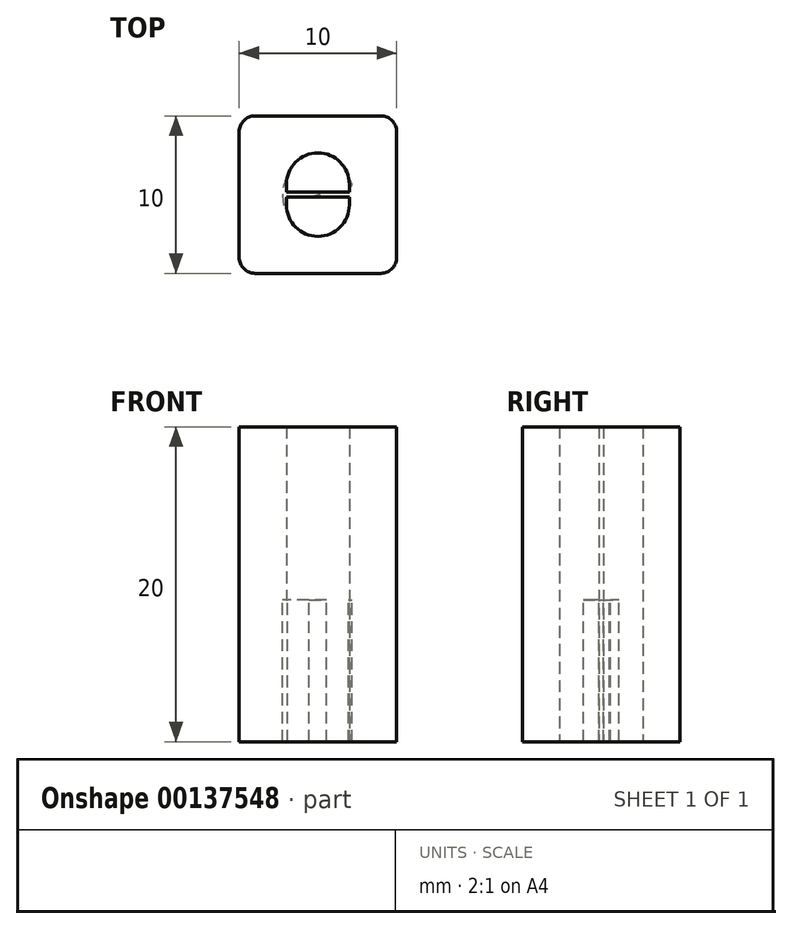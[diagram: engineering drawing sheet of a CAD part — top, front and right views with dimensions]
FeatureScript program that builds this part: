
annotation { "Feature Type Name" : "Feature", "Feature Type Description" : "" }
export const myFeature = defineFeature(function(context is Context, id is Id, definition is map)
    precondition{}
    {
        {
            var Q0;
            Q0=qCreatedBy(makeId("Top.planeOp"),FACE);
            var sketch = newSketch(context, id + "F0", { "sketchPlane" : qUnion([Q0])});
            skLineSegment(sketch, "E0.rect.bottom", {"start": v(4.45, -5.07) * mm, "end": v(-5.55, -5.07) * mm});
            skLineSegment(sketch, "E0.rect.top", {"start": v(4.45, 4.93) * mm, "end": v(-5.55, 4.93) * mm});
            skLineSegment(sketch, "E0.rect.left", {"start": v(4.45, -5.07) * mm, "end": v(4.45, 4.93) * mm});
            skLineSegment(sketch, "E0.rect.right", {"start": v(-5.55, -5.07) * mm, "end": v(-5.55, 4.93) * mm});
            skPoint(sketch, "E0.rect.middle", {"position": v(-0.55, -0.07) * mm});
            skLineSegment(sketch, "E1.rect.bottom", {"start": v(1.45, -0.22) * mm, "end": v(-2.55, -0.22) * mm});
            skLineSegment(sketch, "E1.rect.top", {"start": v(1.45, 0.08) * mm, "end": v(-2.55, 0.08) * mm});
            skLineSegment(sketch, "E1.rect.left", {"start": v(1.45, -0.22) * mm, "end": v(1.45, 0.08) * mm});
            skLineSegment(sketch, "E1.rect.right", {"start": v(-2.55, -0.22) * mm, "end": v(-2.55, 0.08) * mm});
            skLineSegment(sketch, "E2.bottom", {"start": v(-2.55, -0.22) * mm, "end": v(1.45, -0.22) * mm});
            skLineSegment(sketch, "E2.left", {"start": v(-2.55, -0.22) * mm, "end": v(-2.55, -0.72) * mm});
            skLineSegment(sketch, "E2.right", {"start": v(1.45, -0.22) * mm, "end": v(1.45, -0.72) * mm});
            skLineSegment(sketch, "E3.bottom", {"start": v(-2.55, 0.08) * mm, "end": v(1.45, 0.08) * mm});
            skLineSegment(sketch, "E3.left", {"start": v(-2.55, 0.08) * mm, "end": v(-2.55, 0.58) * mm});
            skLineSegment(sketch, "E3.right", {"start": v(1.45, 0.08) * mm, "end": v(1.45, 0.58) * mm});
            skArc(sketch, "E4", {"start": v(-2.55, -0.72) * mm, "mid": v(-0.55, -2.72) * mm, "end": v(1.45, -0.72) * mm});
            skArc(sketch, "E5", {"start": v(1.45, 0.58) * mm, "mid": v(-0.55, 2.58) * mm, "end": v(-2.55, 0.58) * mm});
            skLineSegment(sketch, "E6", {"start": v(-0.55, -5.07) * mm, "end": v(-0.55, 4.93) * mm, "construction": true});
            skSolve(sketch);
        }
        {
            var Q0;
            Q0=makeQuery(id+"F0.imprint","IMPRINT",FACE,{"disambiguationData":[TD([[makeQuery(id+"F0.imprint","IMPRINT",EDGE,{"derivedFrom":sQuery(id+"F0.wireOp",EDGE,"E0.rect.bottom")}),-1.0]])]});
            var Q1;
            Q1=makeQuery(id+"F0.imprint","IMPRINT",FACE,{"disambiguationData":[TD([[makeQuery(id+"F0.imprint","IMPRINT",EDGE,{"derivedFrom":sQuery(id+"F0.wireOp",EDGE,"E1.rect.left")}),1.0]])]});
            extrude(context, id + "F1", {"entities" : qUnion([Q0, Q1]), "depth" : 9 * mm});
        }
        {
            var Q0;
            Q0=makeQuery(id+"F0.imprint","IMPRINT",FACE,{"disambiguationData":[TD([[makeQuery(id+"F0.imprint","IMPRINT",EDGE,{"derivedFrom":sQuery(id+"F0.wireOp",EDGE,"E0.rect.bottom")}),-1.0]])]});
            var Q1;
            Q1=makeQuery(id+"F0.imprint","IMPRINT",FACE,{"disambiguationData":[TD([[makeQuery(id+"F0.imprint","IMPRINT",EDGE,{"derivedFrom":sQuery(id+"F0.wireOp",EDGE,"E2.bottom")}),-1.0]])]});
            var Q2;
            Q2=makeQuery(id+"F0.imprint","IMPRINT",FACE,{"disambiguationData":[TD([[makeQuery(id+"F0.imprint","IMPRINT",EDGE,{"derivedFrom":sQuery(id+"F0.wireOp",EDGE,"E1.rect.left")}),1.0]])]});
            var Q3;
            Q3=makeQuery(id+"F0.imprint","IMPRINT",FACE,{"disambiguationData":[TD([[makeQuery(id+"F0.imprint","IMPRINT",EDGE,{"derivedFrom":sQuery(id+"F0.wireOp",EDGE,"E3.bottom")}),1.0]])]});
            extrude(context, id + "F2", {"entities" : qUnion([Q0, Q1, Q2, Q3]), "operationType" : NewBodyOperationType.ADD, "oppositeDirection" : true, "depth" : 2 * mm});
        }
        {
            var Q0;
            Q0=makeQuery(id+"F2.opExtrude","CAP_FACE",FACE,{"disambiguationData":[OSD([sQuery(id+"F0.wireOp",EDGE,"E0.rect.bottom"),sQuery(id+"F0.wireOp",EDGE,"E0.rect.top"),sQuery(id+"F0.wireOp",EDGE,"E0.rect.left"),sQuery(id+"F0.wireOp",EDGE,"E0.rect.right")])],"isStart":false});
            var sketch = newSketch(context, id + "F3", { "sketchPlane" : qUnion([Q0])});
            skCircle(sketch, "E7", {"center": v(-0.55, 0.07) * mm, "radius": 2.25 * mm});
            skLineSegment(sketch, "E8", {"start": v(-0.55, 5.07) * mm, "end": v(-0.55, -4.93) * mm, "construction": true});
            skLineSegment(sketch, "E9", {"start": v(-2.72, 0.66) * mm, "end": v(1.63, -0.5) * mm});
            skSolve(sketch);
        }
        {
            var Q0;
            Q0=makeQuery(id+"F3.imprint","IMPRINT",FACE,{"disambiguationData":[TD([[makeQuery(id+"F3.imprint","IMPRINT",EDGE,{"derivedFrom":makeQuery(id+"F2.opExtrude","CAP_EDGE",EDGE,{"disambiguationData":[OSD([sQuery(id+"F0.wireOp",EDGE,"E0.rect.bottom")])],"isStart":false})}),1.0]])]});
            var Q1;
            {var subQ0=sQuery(id+"F3.wireOp",EDGE,"E9");Q1=makeQuery(id+"F3.imprint","IMPRINT",FACE,{"disambiguationData":[TD([[makeQuery(id+"F3.imprint","IMPRINT",EDGE,{"derivedFrom":subQ0}),1.0]])]});}
            extrude(context, id + "F4", {"entities" : qUnion([Q0, Q1]), "depth" : 9 * mm});
        }
        {
            var Q0;
            Q0=makeQuery(id+"F1.opExtrude","SWEPT_BODY",BODY,{"disambiguationData":[OSD([sQuery(id+"F0.wireOp",EDGE,"E0.rect.bottom"),sQuery(id+"F0.wireOp",EDGE,"E0.rect.top"),sQuery(id+"F0.wireOp",EDGE,"E0.rect.left"),sQuery(id+"F0.wireOp",EDGE,"E0.rect.right"),sQuery(id+"F0.wireOp",EDGE,"E2.bottom"),sQuery(id+"F0.wireOp",EDGE,"E2.left"),sQuery(id+"F0.wireOp",EDGE,"E2.right"),sQuery(id+"F0.wireOp",EDGE,"E3.bottom"),sQuery(id+"F0.wireOp",EDGE,"E3.left"),sQuery(id+"F0.wireOp",EDGE,"E3.right"),sQuery(id+"F0.wireOp",EDGE,"E4"),sQuery(id+"F0.wireOp",EDGE,"E5")])]});
            var Q1;
            Q1=makeQuery(id+"F4.opExtrude","SWEPT_BODY",BODY,{"disambiguationData":[OSD([sQuery(id+"F0.wireOp",EDGE,"E0.rect.bottom"),sQuery(id+"F0.wireOp",EDGE,"E0.rect.top"),sQuery(id+"F0.wireOp",EDGE,"E0.rect.left"),sQuery(id+"F0.wireOp",EDGE,"E0.rect.right"),sQuery(id+"F3.wireOp",EDGE,"E7"),sQuery(id+"F3.wireOp",EDGE,"jH7qDuqV-ohNc-biuR-j1ed-sVB3w5zqeR1x")])]});
            booleanBodies(context, id + "F5", {"operationType" : BooleanOperationType.UNION, "tools" : qUnion([Q0, Q1])});
        }
        {
            var Q0;
            {var subQ0=sQuery(id+"F0.wireOp",EDGE,"E0.rect.right");var subQ1=sQuery(id+"F0.wireOp",EDGE,"E0.rect.top");Q0=makeQuery(id+"F5.opBoolean","MERGE",EDGE,{"derivedFrom":[makeQuery(id+"F2.boolean.opBoolean","MERGE",EDGE,{"derivedFrom":[makeQuery(id+"F1.opExtrude","SWEPT_EDGE",EDGE,{"disambiguationData":[OSD([subQ1,subQ0])]}),makeQuery(id+"F2.opExtrude","SWEPT_EDGE",EDGE,{"disambiguationData":[OSD([subQ1,subQ0])]})]}),makeQuery(id+"F4.opExtrude","SWEPT_EDGE",EDGE,{"disambiguationData":[OSD([subQ1,subQ0])]})]});}
            var Q1;
            {var subQ0=sQuery(id+"F0.wireOp",EDGE,"E0.rect.left");var subQ1=sQuery(id+"F0.wireOp",EDGE,"E0.rect.top");Q1=makeQuery(id+"F5.opBoolean","MERGE",EDGE,{"derivedFrom":[makeQuery(id+"F2.boolean.opBoolean","MERGE",EDGE,{"derivedFrom":[makeQuery(id+"F1.opExtrude","SWEPT_EDGE",EDGE,{"disambiguationData":[OSD([subQ1,subQ0])]}),makeQuery(id+"F2.opExtrude","SWEPT_EDGE",EDGE,{"disambiguationData":[OSD([subQ1,subQ0])]})]}),makeQuery(id+"F4.opExtrude","SWEPT_EDGE",EDGE,{"disambiguationData":[OSD([subQ1,subQ0])]})]});}
            var Q2;
            {var subQ0=sQuery(id+"F0.wireOp",EDGE,"E0.rect.left");var subQ1=sQuery(id+"F0.wireOp",EDGE,"E0.rect.bottom");Q2=makeQuery(id+"F5.opBoolean","MERGE",EDGE,{"derivedFrom":[makeQuery(id+"F2.boolean.opBoolean","MERGE",EDGE,{"derivedFrom":[makeQuery(id+"F1.opExtrude","SWEPT_EDGE",EDGE,{"disambiguationData":[OSD([subQ1,subQ0])]}),makeQuery(id+"F2.opExtrude","SWEPT_EDGE",EDGE,{"disambiguationData":[OSD([subQ1,subQ0])]})]}),makeQuery(id+"F4.opExtrude","SWEPT_EDGE",EDGE,{"disambiguationData":[OSD([subQ1,subQ0])]})]});}
            var Q3;
            {var subQ0=sQuery(id+"F0.wireOp",EDGE,"E0.rect.right");var subQ1=sQuery(id+"F0.wireOp",EDGE,"E0.rect.bottom");Q3=makeQuery(id+"F5.opBoolean","MERGE",EDGE,{"derivedFrom":[makeQuery(id+"F2.boolean.opBoolean","MERGE",EDGE,{"derivedFrom":[makeQuery(id+"F1.opExtrude","SWEPT_EDGE",EDGE,{"disambiguationData":[OSD([subQ1,subQ0])]}),makeQuery(id+"F2.opExtrude","SWEPT_EDGE",EDGE,{"disambiguationData":[OSD([subQ1,subQ0])]})]}),makeQuery(id+"F4.opExtrude","SWEPT_EDGE",EDGE,{"disambiguationData":[OSD([subQ1,subQ0])]})]});}
            fillet(context, id + "F6", {"entities" : qUnion([Q0, Q1, Q2, Q3]), "radius" : 1 * mm, "tangentPropagation" : true, "allowEdgeOverflow" : false});
        }
    });
